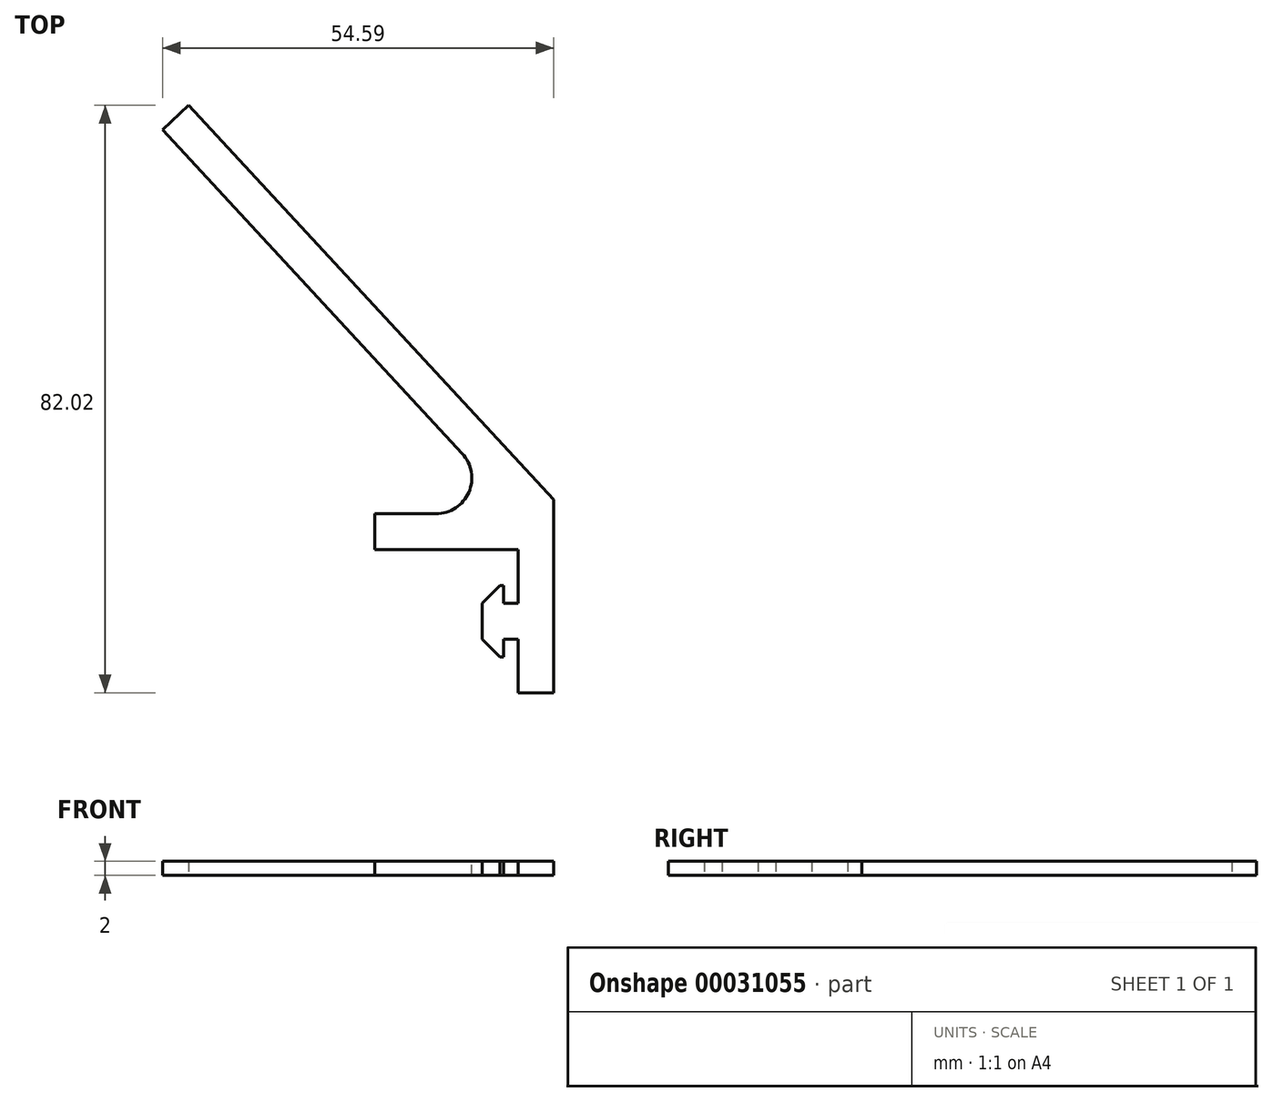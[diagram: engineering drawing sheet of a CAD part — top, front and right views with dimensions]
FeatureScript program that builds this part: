
annotation { "Feature Type Name" : "Feature", "Feature Type Description" : "" }
export const myFeature = defineFeature(function(context is Context, id is Id, definition is map)
    precondition{}
    {
        {
            var Q0;
            Q0=qCreatedBy(makeId("Top.planeOp"),FACE);
            var sketch = newSketch(context, id + "F0", { "sketchPlane" : qUnion([Q0])});
            skLineSegment(sketch, "E0", {"start": v(-27.9, 31.82) * mm, "end": v(-7.9, 31.82) * mm});
            skLineSegment(sketch, "E1", {"start": v(-7.9, 31.82) * mm, "end": v(-7.9, 24.32) * mm});
            skLineSegment(sketch, "E2", {"start": v(-7.9, 24.32) * mm, "end": v(-9.9, 24.32) * mm});
            skLineSegment(sketch, "E3", {"start": v(-9.9, 24.32) * mm, "end": v(-9.9, 26.82) * mm});
            skLineSegment(sketch, "E4", {"start": v(-9.9, 26.82) * mm, "end": v(-10.4, 26.82) * mm});
            skLineSegment(sketch, "E5", {"start": v(-10.4, 26.82) * mm, "end": v(-12.9, 24.32) * mm});
            skLineSegment(sketch, "E6", {"start": v(-12.9, 24.32) * mm, "end": v(-12.9, 19.32) * mm});
            skLineSegment(sketch, "E7", {"start": v(-12.9, 19.32) * mm, "end": v(-10.4, 16.82) * mm});
            skLineSegment(sketch, "E8", {"start": v(-10.4, 16.82) * mm, "end": v(-9.9, 16.82) * mm});
            skLineSegment(sketch, "E9", {"start": v(-9.9, 16.82) * mm, "end": v(-9.9, 19.32) * mm});
            skLineSegment(sketch, "E10", {"start": v(-9.9, 19.32) * mm, "end": v(-7.9, 19.32) * mm});
            skLineSegment(sketch, "E11", {"start": v(-7.9, 19.32) * mm, "end": v(-7.9, 11.82) * mm});
            skLineSegment(sketch, "E12", {"start": v(-7.9, 11.82) * mm, "end": v(-2.9, 11.82) * mm});
            skLineSegment(sketch, "E13", {"start": v(-2.9, 11.82) * mm, "end": v(-2.9, 38.77) * mm});
            skLineSegment(sketch, "E14", {"start": v(-2.9, 38.77) * mm, "end": v(-53.82, 93.84) * mm});
            skLineSegment(sketch, "E15", {"start": v(-53.82, 93.84) * mm, "end": v(-57.5, 90.44) * mm});
            skLineSegment(sketch, "E16", {"start": v(-57.5, 90.44) * mm, "end": v(-7.9, 36.82) * mm});
            skLineSegment(sketch, "E17", {"start": v(-7.9, 36.82) * mm, "end": v(-27.9, 36.82) * mm});
            skLineSegment(sketch, "E18", {"start": v(-27.9, 36.82) * mm, "end": v(-27.9, 31.82) * mm});
            skSolve(sketch);
        }
        {
            var Q0;
            Q0=makeQuery(id+"F0.imprint","IMPRINT",FACE,{"disambiguationData":[TD([[makeQuery(id+"F0.imprint","IMPRINT",EDGE,{"derivedFrom":sQuery(id+"F0.wireOp",EDGE,"E0")}),1.0]])]});
            extrude(context, id + "F1", {"entities" : qUnion([Q0]), "depth" : 2 * mm});
        }
        {
            var Q0;
            Q0=makeQuery(id+"F1.opExtrude","SWEPT_EDGE",EDGE,{"disambiguationData":[OSD([sQuery(id+"F0.wireOp",EDGE,"E16"),sQuery(id+"F0.wireOp",EDGE,"E17")])]});
            fillet(context, id + "F2", {"entities" : qUnion([Q0]), "radius" : 5 * mm, "tangentPropagation" : true, "allowEdgeOverflow" : false});
        }
    });
